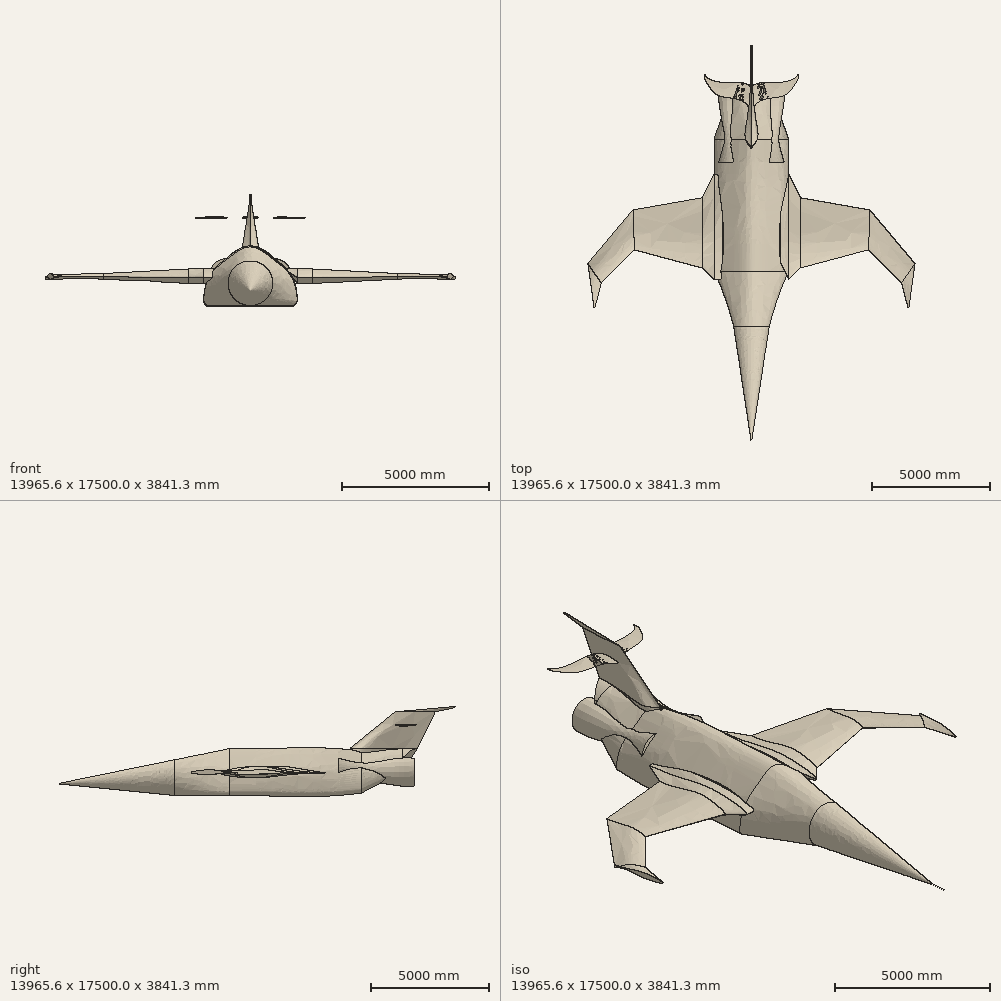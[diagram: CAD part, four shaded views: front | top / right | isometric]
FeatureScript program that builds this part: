
annotation { "Feature Type Name" : "Feature", "Feature Type Description" : "" }
export const myFeature = defineFeature(function(context is Context, id is Id, definition is map)
    precondition{}
    {
        {
            var Q0;
            Q0=qCreatedBy(makeId("Right.planeOp"),FACE);
            var sketch = newSketch(context, id + "F0", { "sketchPlane" : qUnion([Q0])});
            skLineSegment(sketch, "E0", {"start": v(0, 0) * mm, "end": v(-1750, 0) * mm});
            skLineSegment(sketch, "E1", {"start": v(-1750, 0) * mm, "end": v(-3500, 0) * mm});
            skLineSegment(sketch, "E2", {"start": v(-3500, 0) * mm, "end": v(-3500, -1000) * mm});
            skLineSegment(sketch, "E3", {"start": v(-3500, -1000) * mm, "end": v(-8500, -1000) * mm});
            skLineSegment(sketch, "E4", {"start": v(-8500, -1000) * mm, "end": v(-8500, -499.31) * mm});
            skLineSegment(sketch, "E5", {"start": v(-1151.4, 0) * mm, "end": v(-1151.4, 1000) * mm});
            skLineSegment(sketch, "E6", {"start": v(-1151.4, 1000) * mm, "end": v(-8500, -499.31) * mm});
            skLineSegment(sketch, "E7", {"start": v(-8500, -499.31) * mm, "end": v(-3500, -1000) * mm});
            skLineSegment(sketch, "E8", {"start": v(-3500, 0) * mm, "end": v(-3500, 520.82) * mm});
            skLineSegment(sketch, "E9", {"start": v(-8500, -499.31) * mm, "end": v(-8450, -499.31) * mm});
            skLineSegment(sketch, "E10", {"start": v(-8450, -499.31) * mm, "end": v(-8450, -489.1) * mm});
            skLineSegment(sketch, "E11", {"start": v(-8450, -499.31) * mm, "end": v(-8450, -504.32) * mm});
            skSolve(sketch);
        }
        {
            var Q0;
            Q0=sQuery(id+"F0.wireOp",EDGE,"E5");
            cPlane(context, id + "F1", {"entities" : qUnion([Q0]), "cplaneType" : CPlaneType.LINE_ANGLE, "offset" : 25 * mm, "angle" : 90 * degree, "oppositeDirection" : true, "width" : 150 * mm, "height" : 150 * mm});
        }
        {
            var Q0;
            Q0=qCreatedBy(id+"F1.planeOp",FACE);
            var sketch = newSketch(context, id + "F2", { "sketchPlane" : qUnion([Q0])});
            skLineSegment(sketch, "E12.top", {"start": v(-1394.2, -1000) * mm, "end": v(1394.2, -1000) * mm});
            skPoint(sketch, "E12.middle", {"position": v(0, 0) * mm});
            skFitSpline(sketch, "E13", {"points": [v(-1600, -1000) * mm, v(-848, 530) * mm, v(0, 1000) * mm, v(848, 530) * mm, v(1600, -1000) * mm], "startDerivative": vector(0, 10524.75) * mm, "endDerivative": vector(0, -10524.75) * mm});
            skArc(sketch, "E14", {"start": v(-735.27, 618.52) * mm, "mid": v(-1273.27, 435.52) * mm, "end": v(-1440.68, -107.53) * mm});
            skArc(sketch, "E15", {"start": v(1440.68, -107.53) * mm, "mid": v(1273.27, 435.52) * mm, "end": v(735.27, 618.52) * mm});
            skFitSpline(sketch, "E16.trimOffspring", {"points": [v(-1600, -1000) * mm, v(-848, 530) * mm, v(0, 1000) * mm, v(848, 530) * mm, v(1600, -1000) * mm], "startDerivative": vector(0, 10524.75) * mm, "endDerivative": vector(0, -10524.75) * mm});
            skFitSpline(sketch, "E17.trimOffspring", {"points": [v(-1600, -1000) * mm, v(-848, 530) * mm, v(0, 1000) * mm, v(848, 530) * mm, v(1600, -1000) * mm], "startDerivative": vector(0, 10524.75) * mm, "endDerivative": vector(0, -10524.75) * mm});
            skArc(sketch, "E18.filletArc", {"start": v(-1593.82, -787.83) * mm, "mid": v(-1539.85, -937.05) * mm, "end": v(-1394.2, -1000) * mm});
            skArc(sketch, "E19.filletArc", {"start": v(1394.2, -1000) * mm, "mid": v(1539.85, -937.05) * mm, "end": v(1593.82, -787.83) * mm});
            skSolve(sketch);
        }
        {
            var Q0;
            Q0=qCreatedBy(makeId("Front.planeOp"),FACE);
            var sketch = newSketch(context, id + "F3", { "sketchPlane" : qUnion([Q0])});
            skLineSegment(sketch, "E20.top", {"start": v(-1394.2, -1000) * mm, "end": v(1394.2, -1000) * mm});
            skPoint(sketch, "E20.middle", {"position": v(0, 0) * mm});
            skFitSpline(sketch, "E21", {"points": [v(-1600, -1000) * mm, v(-848, 530) * mm, v(0, 1000) * mm, v(848, 530) * mm, v(1600, -1000) * mm], "startDerivative": vector(0, 10524.75) * mm, "endDerivative": vector(0, -10524.75) * mm});
            skArc(sketch, "E22", {"start": v(-735.27, 618.52) * mm, "mid": v(-1273.27, 435.52) * mm, "end": v(-1440.68, -107.53) * mm});
            skArc(sketch, "E23", {"start": v(1440.68, -107.53) * mm, "mid": v(1273.27, 435.52) * mm, "end": v(735.27, 618.52) * mm});
            skFitSpline(sketch, "E24.trimOffspring", {"points": [v(-1600, -1000) * mm, v(-848, 530) * mm, v(0, 1000) * mm, v(848, 530) * mm, v(1600, -1000) * mm], "startDerivative": vector(0, 10524.75) * mm, "endDerivative": vector(0, -10524.75) * mm});
            skFitSpline(sketch, "E25.trimOffspring", {"points": [v(-1600, -1000) * mm, v(-848, 530) * mm, v(0, 1000) * mm, v(848, 530) * mm, v(1600, -1000) * mm], "startDerivative": vector(0, 10524.75) * mm, "endDerivative": vector(0, -10524.75) * mm});
            skArc(sketch, "E26.filletArc", {"start": v(-1593.82, -787.83) * mm, "mid": v(-1539.85, -937.05) * mm, "end": v(-1394.2, -1000) * mm});
            skArc(sketch, "E27.filletArc", {"start": v(1394.2, -1000) * mm, "mid": v(1539.85, -937.05) * mm, "end": v(1593.82, -787.83) * mm});
            skSolve(sketch);
        }
        {
            var Q0;
            Q0=qCreatedBy(makeId("Front.planeOp"),FACE);
            cPlane(context, id + "F4", {"entities" : qUnion([Q0]), "cplaneType" : CPlaneType.OFFSET, "offset" : 3500 * mm, "oppositeDirection" : true, "width" : 150 * mm, "height" : 150 * mm});
        }
        {
            var Q0;
            Q0=qCreatedBy(id+"F4.planeOp",FACE);
            var sketch = newSketch(context, id + "F5", { "sketchPlane" : qUnion([Q0])});
            skLineSegment(sketch, "E28.top", {"start": v(-1394.2, -1000) * mm, "end": v(1394.2, -1000) * mm});
            skPoint(sketch, "E28.middle", {"position": v(0, 0) * mm});
            skFitSpline(sketch, "E29", {"points": [v(-1600, -1000) * mm, v(-848, 530) * mm, v(0, 1000) * mm, v(848, 530) * mm, v(1600, -1000) * mm], "startDerivative": vector(0, 10524.75) * mm, "endDerivative": vector(0, -10524.75) * mm});
            skArc(sketch, "E30", {"start": v(-735.27, 618.52) * mm, "mid": v(-1273.27, 435.52) * mm, "end": v(-1440.68, -107.53) * mm});
            skArc(sketch, "E31", {"start": v(1440.68, -107.53) * mm, "mid": v(1273.27, 435.52) * mm, "end": v(735.27, 618.52) * mm});
            skFitSpline(sketch, "E32.trimOffspring", {"points": [v(-1600, -1000) * mm, v(-848, 530) * mm, v(0, 1000) * mm, v(848, 530) * mm, v(1600, -1000) * mm], "startDerivative": vector(0, 10524.75) * mm, "endDerivative": vector(0, -10524.75) * mm});
            skFitSpline(sketch, "E33.trimOffspring", {"points": [v(-1600, -1000) * mm, v(-848, 530) * mm, v(0, 1000) * mm, v(848, 530) * mm, v(1600, -1000) * mm], "startDerivative": vector(0, 10524.75) * mm, "endDerivative": vector(0, -10524.75) * mm});
            skArc(sketch, "E34.filletArc", {"start": v(-1593.82, -787.83) * mm, "mid": v(-1539.85, -937.05) * mm, "end": v(-1394.2, -1000) * mm});
            skArc(sketch, "E35.filletArc", {"start": v(1394.2, -1000) * mm, "mid": v(1539.85, -937.05) * mm, "end": v(1593.82, -787.83) * mm});
            skSolve(sketch);
        }
        {
            var Q0;
            Q0=qCreatedBy(makeId("Front.planeOp"),FACE);
            cPlane(context, id + "F6", {"entities" : qUnion([Q0]), "cplaneType" : CPlaneType.OFFSET, "offset" : 4500 * mm, "oppositeDirection" : true, "width" : 150 * mm, "height" : 150 * mm});
        }
        {
            var Q0;
            Q0=qCreatedBy(id+"F6.planeOp",FACE);
            var sketch = newSketch(context, id + "F7", { "sketchPlane" : qUnion([Q0])});
            skLineSegment(sketch, "E36.top", {"start": v(-1413.07, -900) * mm, "end": v(1413.07, -900) * mm});
            skPoint(sketch, "E36.middle", {"position": v(0, 0) * mm});
            skFitSpline(sketch, "E37", {"points": [v(-1600, -900) * mm, v(-784.42, 441.24) * mm, v(0, 900) * mm, v(784.42, 441.24) * mm, v(1600, -900) * mm], "startDerivative": vector(0, 9508.62) * mm, "endDerivative": vector(0, -9508.62) * mm});
            skArc(sketch, "E38", {"start": v(-719.25, 488.69) * mm, "mid": v(-1131.76, 394.84) * mm, "end": v(-1324.66, 18.33) * mm});
            skArc(sketch, "E39", {"start": v(1324.66, 18.33) * mm, "mid": v(1131.76, 394.84) * mm, "end": v(719.25, 488.69) * mm});
            skFitSpline(sketch, "E40.trimOffspring", {"points": [v(-1600, -900) * mm, v(-784.42, 441.24) * mm, v(0, 900) * mm, v(784.42, 441.24) * mm, v(1600, -900) * mm], "startDerivative": vector(0, 9508.62) * mm, "endDerivative": vector(0, -9508.62) * mm});
            skFitSpline(sketch, "E41.trimOffspring", {"points": [v(-1600, -900) * mm, v(-784.42, 441.24) * mm, v(0, 900) * mm, v(784.42, 441.24) * mm, v(1600, -900) * mm], "startDerivative": vector(0, 9508.62) * mm, "endDerivative": vector(0, -9508.62) * mm});
            skArc(sketch, "E42.filletArc", {"start": v(-1592.48, -705.43) * mm, "mid": v(-1545.4, -842.02) * mm, "end": v(-1413.07, -900) * mm});
            skArc(sketch, "E43.filletArc", {"start": v(1413.07, -900) * mm, "mid": v(1545.4, -842.02) * mm, "end": v(1592.48, -705.43) * mm});
            skLineSegment(sketch, "E44", {"start": v(-719.25, 488.69) * mm, "end": v(-1324.66, 18.33) * mm, "construction": true});
            skLineSegment(sketch, "E45", {"start": v(719.25, 488.69) * mm, "end": v(1324.66, 18.33) * mm, "construction": true});
            skSolve(sketch);
        }
        {
            var Q0;
            Q0=qCreatedBy(makeId("Front.planeOp"),FACE);
            cPlane(context, id + "F8", {"entities" : qUnion([Q0]), "cplaneType" : CPlaneType.OFFSET, "offset" : 6232.05 * mm, "oppositeDirection" : true, "width" : 150 * mm, "height" : 150 * mm});
        }
        {
            var Q0;
            Q0=qCreatedBy(id+"F8.planeOp",FACE);
            var sketch = newSketch(context, id + "F9", { "sketchPlane" : qUnion([Q0])});
            skArc(sketch, "E46", {"start": v(998.61, 52.63) * mm, "mid": v(0, 1000) * mm, "end": v(-998.61, 52.63) * mm});
            skLineSegment(sketch, "E47", {"start": v(0, 0) * mm, "end": v(-948.68, 0) * mm});
            skLineSegment(sketch, "E48", {"start": v(0, 0) * mm, "end": v(948.68, 0) * mm});
            skLineSegment(sketch, "E49", {"start": v(0, 1000) * mm, "end": v(0, 675) * mm, "construction": true});
            skLineSegment(sketch, "E50", {"start": v(0, 675) * mm, "end": v(-737.82, 675) * mm, "construction": true});
            skLineSegment(sketch, "E51", {"start": v(0, 675) * mm, "end": v(737.82, 675) * mm, "construction": true});
            skPoint(sketch, "E52.visualSharp", {"position": v(-1000, 0) * mm});
            skArc(sketch, "E52.filletArc", {"start": v(-998.61, 52.63) * mm, "mid": v(-984.96, 15.59) * mm, "end": v(-948.68, 0) * mm});
            skPoint(sketch, "E53.visualSharp", {"position": v(1000, 0) * mm});
            skArc(sketch, "E53.filletArc", {"start": v(948.68, 0) * mm, "mid": v(984.96, 15.59) * mm, "end": v(998.61, 52.63) * mm});
            skSolve(sketch);
        }
        {
            var Q0;
            Q0=makeQuery(id+"F2.imprint","IMPRINT",FACE,{"disambiguationData":[TD([[makeQuery(id+"F2.imprint","IMPRINT",EDGE,{"derivedFrom":sQuery(id+"F2.wireOp",EDGE,"E12.top")}),1.0]])]});
            var Q1;
            Q1=makeQuery(id+"F3.imprint","IMPRINT",FACE,{"disambiguationData":[TD([[makeQuery(id+"F3.imprint","IMPRINT",EDGE,{"derivedFrom":sQuery(id+"F3.wireOp",EDGE,"E20.top")}),1.0]])]});
            var Q2;
            Q2=makeQuery(id+"F5.imprint","IMPRINT",FACE,{"disambiguationData":[TD([[makeQuery(id+"F5.imprint","IMPRINT",EDGE,{"derivedFrom":sQuery(id+"F5.wireOp",EDGE,"E28.top")}),1.0]])]});
            var Q3;
            Q3=makeQuery(id+"F7.imprint","IMPRINT",FACE,{"disambiguationData":[TD([[makeQuery(id+"F7.imprint","IMPRINT",EDGE,{"derivedFrom":sQuery(id+"F7.wireOp",EDGE,"E36.top")}),1.0]])]});
            loft(context, id + "F10", {"sheetProfilesArray" : [{ "sheetProfileEntities" : qUnion([Q0]) }, { "sheetProfileEntities" : qUnion([Q1]) }, { "sheetProfileEntities" : qUnion([Q2]) }, { "sheetProfileEntities" : qUnion([Q3]) }]});
        }
        {
            var Q0;
            Q0=sQuery(id+"F7.wireOp",EDGE,"E44");
            var Q1;
            Q1=sQuery(id+"F9.wireOp",VERTEX,"E50.end");
            cPlane(context, id + "F11", {"entities" : qUnion([Q0, Q1]), "cplaneType" : CPlaneType.LINE_ANGLE, "offset" : 25 * mm, "angle" : 180 * degree, "width" : 150 * mm, "height" : 150 * mm});
        }
        {
            var Q0;
            Q0=qCreatedBy(id+"F11.planeOp",FACE);
            var sketch = newSketch(context, id + "F12", { "sketchPlane" : qUnion([Q0])});
            skLineSegment(sketch, "E54", {"start": v(-589.34, 4526.34) * mm, "end": v(-612.8, 6268.32) * mm});
            skLineSegment(sketch, "E55", {"start": v(-1354.08, 4472.19) * mm, "end": v(-612.8, 6268.32) * mm});
            skSolve(sketch);
        }
        {
            var Q0;
            Q0=sQuery(id+"F7.wireOp",EDGE,"E45");
            var Q1;
            Q1=sQuery(id+"F9.wireOp",VERTEX,"E51.end");
            cPlane(context, id + "F13", {"entities" : qUnion([Q0, Q1]), "cplaneType" : CPlaneType.LINE_ANGLE, "offset" : 25 * mm, "angle" : 0 * degree, "width" : 150 * mm, "height" : 150 * mm});
        }
        {
            var Q0;
            Q0=qCreatedBy(id+"F13.planeOp",FACE);
            var sketch = newSketch(context, id + "F14", { "sketchPlane" : qUnion([Q0])});
            skLineSegment(sketch, "E56", {"start": v(589.34, 4526.34) * mm, "end": v(612.8, 6268.32) * mm});
            skLineSegment(sketch, "E57", {"start": v(1354.08, 4472.19) * mm, "end": v(612.8, 6268.32) * mm});
            skSolve(sketch);
        }
        {
            var Q1;
            Q1=makeQuery(id+"F10.opLoft","CAP_FACE",FACE,{"disambiguationData":[OSD([makeQuery(id+"F7.imprint","IMPRINT",FACE,{"disambiguationData":[TD([[makeQuery(id+"F7.imprint","IMPRINT",EDGE,{"derivedFrom":sQuery(id+"F7.wireOp",EDGE,"E36.top")}),1.0]])]})])],"isStart":true});
            var Q2;
            Q2=makeQuery(id+"F9.imprint","IMPRINT",FACE,{"disambiguationData":[TD([[makeQuery(id+"F9.imprint","IMPRINT",EDGE,{"derivedFrom":sQuery(id+"F9.wireOp",EDGE,"E46")}),1.0]])]});
            var Q3;
            Q3=sQuery(id+"F12.wireOp",EDGE,"E54");
            var Q4;
            Q4=sQuery(id+"F14.wireOp",EDGE,"E56");
            loft(context, id + "F15", {"operationType" : NewBodyOperationType.ADD, "addGuides" : true, "sheetProfilesArray" : [{ "sheetProfileEntities" : qUnion([Q1]) }, { "sheetProfileEntities" : qUnion([Q2]) }], "guidesArray" : [{ "guideEntities" : qUnion([Q3]), "guideDerivativeType" : LoftGuideDerivativeType.DEFAULT, "guideDerivativeMagnitude" : 1 }, { "guideEntities" : qUnion([Q4]), "guideDerivativeType" : LoftGuideDerivativeType.DEFAULT, "guideDerivativeMagnitude" : 1 }]});
        }
        {
            var Q0;
            Q0=makeQuery(id+"F15.opLoft","CAP_FACE",FACE,{"disambiguationData":[OSD([makeQuery(id+"F9.imprint","IMPRINT",FACE,{"disambiguationData":[TD([[makeQuery(id+"F9.imprint","IMPRINT",EDGE,{"derivedFrom":sQuery(id+"F9.wireOp",EDGE,"E46")}),1.0]])]})])],"isStart":true});
            extrude(context, id + "F16", {"entities" : qUnion([Q0]), "operationType" : NewBodyOperationType.ADD, "depth" : 649.4 * mm, "offsetDistance" : 25 * mm});
        }
        {
            var Q0;
            Q0=qCreatedBy(makeId("Right.planeOp"),FACE);
            var sketch = newSketch(context, id + "F17", { "sketchPlane" : qUnion([Q0])});
            skLineSegment(sketch, "E58", {"start": v(0, 0) * mm, "end": v(4500, 0) * mm});
            skLineSegment(sketch, "E59", {"start": v(4500, 0) * mm, "end": v(6232.05, 0) * mm});
            skLineSegment(sketch, "E60", {"start": v(4500, 0) * mm, "end": v(4500, 1000) * mm});
            skLineSegment(sketch, "E61", {"start": v(4500, 1000) * mm, "end": v(6881.46, 1000) * mm});
            skLineSegment(sketch, "E62", {"start": v(6881.46, 1000) * mm, "end": v(6881.46, -1000) * mm});
            skLineSegment(sketch, "E63", {"start": v(6881.46, 1000) * mm, "end": v(6232.05, 0) * mm});
            skLineSegment(sketch, "E64", {"start": v(6232.05, 0) * mm, "end": v(5582.64, -1000) * mm});
            skLineSegment(sketch, "E65", {"start": v(5582.64, -1000) * mm, "end": v(6881.46, -1000) * mm});
            skSolve(sketch);
        }
        {
            var Q0;
            Q0=makeQuery(id+"F17.imprint","IMPRINT",FACE,{"disambiguationData":[TD([[makeQuery(id+"F17.imprint","IMPRINT",EDGE,{"derivedFrom":sQuery(id+"F17.wireOp",EDGE,"E62")}),-1.0]])]});
            var Q1;
            Q1=sQuery(id+"F17.wireOp",EDGE,"E61");
            revolve(context, id + "F18", {"operationType" : NewBodyOperationType.REMOVE, "entities" : qUnion([Q0]), "axis" : qUnion([Q1]), "revolveType" : RevolveType.SYMMETRIC, "oppositeDirection" : true, "angle" : 182 * degree});
        }
        {
            var Q0;
            Q0=qCreatedBy(id+"F1.planeOp",FACE);
            var sketch = newSketch(context, id + "F19", { "sketchPlane" : qUnion([Q0])});
            skLineSegment(sketch, "E66.top", {"start": v(-1394.2, -1000) * mm, "end": v(1394.2, -1000) * mm});
            skPoint(sketch, "E66.middle", {"position": v(0, 0) * mm});
            skFitSpline(sketch, "E67", {"points": [v(-1600, -1000) * mm, v(-848, 530) * mm, v(0, 1000) * mm, v(848, 530) * mm, v(1600, -1000) * mm], "startDerivative": vector(0, 10524.75) * mm, "endDerivative": vector(0, -10524.75) * mm});
            skArc(sketch, "E68.filletArc", {"start": v(-1593.82, -787.83) * mm, "mid": v(-1539.85, -937.05) * mm, "end": v(-1394.2, -1000) * mm});
            skArc(sketch, "E69.filletArc", {"start": v(1394.2, -1000) * mm, "mid": v(1539.85, -937.05) * mm, "end": v(1593.82, -787.83) * mm});
            skLineSegment(sketch, "E70", {"start": v(-1593.82, -787.83) * mm, "end": v(-1394.2, -1000) * mm, "construction": true});
            skLineSegment(sketch, "E71", {"start": v(1593.82, -787.83) * mm, "end": v(1394.2, -1000) * mm, "construction": true});
            skSolve(sketch);
        }
        {
            var Q0;
            Q0=qCreatedBy(makeId("Front.planeOp"),FACE);
            cPlane(context, id + "F20", {"entities" : qUnion([Q0]), "cplaneType" : CPlaneType.OFFSET, "offset" : 3500 * mm, "width" : 150 * mm, "height" : 150 * mm});
        }
        {
            var Q0;
            Q0=qCreatedBy(id+"F20.planeOp",FACE);
            var sketch = newSketch(context, id + "F21", { "sketchPlane" : qUnion([Q0])});
            skCircle(sketch, "E72", {"center": v(0, -239.59) * mm, "radius": 760.41 * mm});
            skLineSegment(sketch, "E73", {"start": v(0, -1000) * mm, "end": v(0, -800) * mm, "construction": true});
            skLineSegment(sketch, "E74", {"start": v(0, -800) * mm, "end": v(-513.97, -800) * mm, "construction": true});
            skLineSegment(sketch, "E75", {"start": v(0, -800) * mm, "end": v(513.97, -800) * mm, "construction": true});
            skSolve(sketch);
        }
        {
            var Q0;
            Q0=qCreatedBy(makeId("Front.planeOp"),FACE);
            cPlane(context, id + "F22", {"entities" : qUnion([Q0]), "cplaneType" : CPlaneType.OFFSET, "offset" : 8450 * mm, "width" : 150 * mm, "height" : 150 * mm});
        }
        {
            var Q0;
            Q0=qCreatedBy(id+"F22.planeOp",FACE);
            var sketch = newSketch(context, id + "F23", { "sketchPlane" : qUnion([Q0])});
            skCircle(sketch, "E76", {"center": v(0, -496.71) * mm, "radius": 7.6 * mm});
            skSolve(sketch);
        }
        {
            var Q0;
            Q0=sQuery(id+"F19.wireOp",EDGE,"E70");
            var Q1;
            Q1=sQuery(id+"F21.wireOp",VERTEX,"E74.end");
            cPlane(context, id + "F24", {"entities" : qUnion([Q0, Q1]), "cplaneType" : CPlaneType.LINE_ANGLE, "offset" : 25 * mm, "angle" : 0 * degree, "width" : 150 * mm, "height" : 150 * mm});
        }
        {
            var Q0;
            Q0=qCreatedBy(id+"F24.planeOp",FACE);
            var sketch = newSketch(context, id + "F25", { "sketchPlane" : qUnion([Q0])});
            skLineSegment(sketch, "E77", {"start": v(3032.27, -230.44) * mm, "end": v(558.11, 518.4) * mm});
            skLineSegment(sketch, "E78", {"start": v(3032.27, -230.44) * mm, "end": v(558.11, 227.09) * mm});
            skSolve(sketch);
        }
        {
            var Q0;
            Q0=sQuery(id+"F19.wireOp",EDGE,"E71");
            var Q1;
            Q1=sQuery(id+"F21.wireOp",VERTEX,"E75.end");
            cPlane(context, id + "F26", {"entities" : qUnion([Q0, Q1]), "cplaneType" : CPlaneType.LINE_ANGLE, "offset" : 25 * mm, "angle" : 180 * degree, "width" : 150 * mm, "height" : 150 * mm});
        }
        {
            var Q0;
            Q0=qCreatedBy(id+"F26.planeOp",FACE);
            var sketch = newSketch(context, id + "F27", { "sketchPlane" : qUnion([Q0])});
            skLineSegment(sketch, "E79", {"start": v(-3032.27, -230.44) * mm, "end": v(-558.11, 518.4) * mm});
            skLineSegment(sketch, "E80", {"start": v(-3032.27, -230.44) * mm, "end": v(-558.11, 227.09) * mm});
            skSolve(sketch);
        }
        {
            var Q1;
            Q1=makeQuery(id+"F19.imprint","IMPRINT",FACE,{"disambiguationData":[TD([[makeQuery(id+"F19.imprint","IMPRINT",EDGE,{"derivedFrom":sQuery(id+"F19.wireOp",EDGE,"E66.top")}),1.0]])]});
            var Q2;
            Q2=makeQuery(id+"F21.imprint","IMPRINT",FACE,{"disambiguationData":[TD([[makeQuery(id+"F21.imprint","IMPRINT",EDGE,{"derivedFrom":sQuery(id+"F21.wireOp",EDGE,"E72")}),1.0]])]});
            var Q3;
            Q3=sQuery(id+"F25.wireOp",EDGE,"E77");
            var Q4;
            Q4=sQuery(id+"F27.wireOp",EDGE,"E79");
            loft(context, id + "F28", {"operationType" : NewBodyOperationType.ADD, "addGuides" : true, "sheetProfilesArray" : [{ "sheetProfileEntities" : qUnion([Q1]) }, { "sheetProfileEntities" : qUnion([Q2]) }], "guidesArray" : [{ "guideEntities" : qUnion([Q3]), "guideDerivativeType" : LoftGuideDerivativeType.DEFAULT, "guideDerivativeMagnitude" : 1 }, { "guideEntities" : qUnion([Q4]), "guideDerivativeType" : LoftGuideDerivativeType.DEFAULT, "guideDerivativeMagnitude" : 1 }]});
        }
        {
            var Q1;
            Q1=makeQuery(id+"F28.opLoft","CAP_FACE",FACE,{"disambiguationData":[OSD([makeQuery(id+"F21.imprint","IMPRINT",FACE,{"disambiguationData":[TD([[makeQuery(id+"F21.imprint","IMPRINT",EDGE,{"derivedFrom":sQuery(id+"F21.wireOp",EDGE,"E72")}),1.0]])]})])],"isStart":true});
            var Q2;
            Q2=makeQuery(id+"F23.imprint","IMPRINT",FACE,{"disambiguationData":[TD([[makeQuery(id+"F23.imprint","IMPRINT",EDGE,{"derivedFrom":sQuery(id+"F23.wireOp",EDGE,"E76")}),1.0]])]});
            loft(context, id + "F29", {"operationType" : NewBodyOperationType.ADD, "sheetProfilesArray" : [{ "sheetProfileEntities" : qUnion([Q1]) }, { "sheetProfileEntities" : qUnion([Q2]) }]});
        }
        {
            var Q0;
            Q0=makeQuery(id+"F29.opLoft","CAP_FACE",FACE,{"disambiguationData":[OSD([makeQuery(id+"F23.imprint","IMPRINT",FACE,{"disambiguationData":[TD([[makeQuery(id+"F23.imprint","IMPRINT",EDGE,{"derivedFrom":sQuery(id+"F23.wireOp",EDGE,"E76")}),1.0]])]})])],"isStart":true});
            extrude(context, id + "F30", {"entities" : qUnion([Q0]), "operationType" : NewBodyOperationType.ADD, "depth" : 550 * mm, "offsetDistance" : 25 * mm});
        }
        {
            var Q0;
            Q0=qCreatedBy(makeId("Front.planeOp"),FACE);
            cPlane(context, id + "F31", {"entities" : qUnion([Q0]), "cplaneType" : CPlaneType.OFFSET, "offset" : 3500 * mm, "oppositeDirection" : true, "width" : 150 * mm, "height" : 150 * mm});
        }
        {
            var Q0;
            Q0=qCreatedBy(id+"F31.planeOp",FACE);
            var sketch = newSketch(context, id + "F32", { "sketchPlane" : qUnion([Q0])});
            skCircle(sketch, "E81", {"center": v(-800, 0) * mm, "radius": 600 * mm});
            skCircle(sketch, "E82", {"center": v(800, 0) * mm, "radius": 600 * mm});
            skSolve(sketch);
        }
        {
            var Q0;
            Q0=qCreatedBy(makeId("Front.planeOp"),FACE);
            cPlane(context, id + "F33", {"entities" : qUnion([Q0]), "cplaneType" : CPlaneType.OFFSET, "offset" : 4500 * mm, "oppositeDirection" : true, "width" : 150 * mm, "height" : 150 * mm});
        }
        {
            var Q0;
            Q0=qCreatedBy(id+"F33.planeOp",FACE);
            var sketch = newSketch(context, id + "F34", { "sketchPlane" : qUnion([Q0])});
            skCircle(sketch, "E83", {"center": v(-800, 0) * mm, "radius": 400 * mm});
            skCircle(sketch, "E84", {"center": v(800, 0) * mm, "radius": 400 * mm});
            skSolve(sketch);
        }
        {
            var Q0;
            Q0=qCreatedBy(makeId("Front.planeOp"),FACE);
            cPlane(context, id + "F35", {"entities" : qUnion([Q0]), "cplaneType" : CPlaneType.OFFSET, "offset" : 6232.05 * mm, "oppositeDirection" : true, "width" : 150 * mm, "height" : 150 * mm});
        }
        {
            var Q0;
            Q0=qCreatedBy(id+"F35.planeOp",FACE);
            var sketch = newSketch(context, id + "F36", { "sketchPlane" : qUnion([Q0])});
            skCircle(sketch, "E85", {"center": v(-800, 0) * mm, "radius": 600 * mm});
            skCircle(sketch, "E86", {"center": v(800, 0) * mm, "radius": 600 * mm});
            skSolve(sketch);
        }
        {
            var Q0;
            Q0=qCreatedBy(makeId("Front.planeOp"),FACE);
            cPlane(context, id + "F37", {"entities" : qUnion([Q0]), "cplaneType" : CPlaneType.OFFSET, "offset" : 6732.05 * mm, "oppositeDirection" : true, "width" : 150 * mm, "height" : 150 * mm});
        }
        {
            var Q0;
            Q0=qCreatedBy(id+"F37.planeOp",FACE);
            var sketch = newSketch(context, id + "F38", { "sketchPlane" : qUnion([Q0])});
            skCircle(sketch, "E87", {"center": v(-800, 0) * mm, "radius": 600 * mm});
            skCircle(sketch, "E88", {"center": v(800, 0) * mm, "radius": 600 * mm});
            skSolve(sketch);
        }
        {
            var Q0;
            Q0=makeQuery(id+"F32.imprint","IMPRINT",FACE,{"disambiguationData":[TD([[makeQuery(id+"F32.imprint","IMPRINT",EDGE,{"derivedFrom":sQuery(id+"F32.wireOp",EDGE,"E81")}),1.0]])]});
            var Q1;
            Q1=makeQuery(id+"F34.imprint","IMPRINT",FACE,{"disambiguationData":[TD([[makeQuery(id+"F34.imprint","IMPRINT",EDGE,{"derivedFrom":sQuery(id+"F34.wireOp",EDGE,"E83")}),1.0]])]});
            var Q2;
            Q2=makeQuery(id+"F36.imprint","IMPRINT",FACE,{"disambiguationData":[TD([[makeQuery(id+"F36.imprint","IMPRINT",EDGE,{"derivedFrom":sQuery(id+"F36.wireOp",EDGE,"E85")}),1.0]])]});
            var Q3;
            Q3=makeQuery(id+"F38.imprint","IMPRINT",FACE,{"disambiguationData":[TD([[makeQuery(id+"F38.imprint","IMPRINT",EDGE,{"derivedFrom":sQuery(id+"F38.wireOp",EDGE,"E87")}),1.0]])]});
            loft(context, id + "F39", {"sheetProfilesArray" : [{ "sheetProfileEntities" : qUnion([Q0]) }, { "sheetProfileEntities" : qUnion([Q1]) }, { "sheetProfileEntities" : qUnion([Q2]) }, { "sheetProfileEntities" : qUnion([Q3]) }]});
        }
        {
            var Q0;
            Q0=makeQuery(id+"F32.imprint","IMPRINT",FACE,{"disambiguationData":[TD([[makeQuery(id+"F32.imprint","IMPRINT",EDGE,{"derivedFrom":sQuery(id+"F32.wireOp",EDGE,"E82")}),1.0]])]});
            var Q1;
            Q1=makeQuery(id+"F34.imprint","IMPRINT",FACE,{"disambiguationData":[TD([[makeQuery(id+"F34.imprint","IMPRINT",EDGE,{"derivedFrom":sQuery(id+"F34.wireOp",EDGE,"E84")}),1.0]])]});
            var Q2;
            Q2=makeQuery(id+"F36.imprint","IMPRINT",FACE,{"disambiguationData":[TD([[makeQuery(id+"F36.imprint","IMPRINT",EDGE,{"derivedFrom":sQuery(id+"F36.wireOp",EDGE,"E86")}),1.0]])]});
            var Q3;
            Q3=makeQuery(id+"F38.imprint","IMPRINT",FACE,{"disambiguationData":[TD([[makeQuery(id+"F38.imprint","IMPRINT",EDGE,{"derivedFrom":sQuery(id+"F38.wireOp",EDGE,"E88")}),1.0]])]});
            loft(context, id + "F40", {"sheetProfilesArray" : [{ "sheetProfileEntities" : qUnion([Q0]) }, { "sheetProfileEntities" : qUnion([Q1]) }, { "sheetProfileEntities" : qUnion([Q2]) }, { "sheetProfileEntities" : qUnion([Q3]) }]});
        }
        {
            var Q0;
            Q0=qCreatedBy(makeId("Top.planeOp"),FACE);
            var sketch = newSketch(context, id + "F41", { "sketchPlane" : qUnion([Q0])});
            skLineSegment(sketch, "E89", {"start": v(0, 0) * mm, "end": v(-1250, 0) * mm});
            skLineSegment(sketch, "E90", {"start": v(-1250, 0) * mm, "end": v(-2100, 0) * mm});
            skLineSegment(sketch, "E91", {"start": v(-2100, 0) * mm, "end": v(-2100, -1000) * mm});
            skLineSegment(sketch, "E92", {"start": v(-2100, 0) * mm, "end": v(-2100, 2000) * mm});
            skLineSegment(sketch, "E93", {"start": v(-2100, -1000) * mm, "end": v(-4997.78, -223.54) * mm});
            skLineSegment(sketch, "E94", {"start": v(-2100, 2000) * mm, "end": v(-5054.42, 1479.06) * mm});
            skLineSegment(sketch, "E95", {"start": v(-4997.78, -223.54) * mm, "end": v(-5054.42, 1479.06) * mm});
            skLineSegment(sketch, "E96", {"start": v(-4997.78, -223.54) * mm, "end": v(-6412, -1637.76) * mm});
            skLineSegment(sketch, "E97", {"start": v(-5054.42, 1479.06) * mm, "end": v(-6982.79, -819.08) * mm});
            skLineSegment(sketch, "E98", {"start": v(-6412, -1637.76) * mm, "end": v(-6982.79, -819.08) * mm});
            skLineSegment(sketch, "E99", {"start": v(-6412, -1637.76) * mm, "end": v(-6704.44, -2799.61) * mm});
            skLineSegment(sketch, "E100", {"start": v(-6704.44, -2799.61) * mm, "end": v(-6982.79, -819.08) * mm});
            skLineSegment(sketch, "E101", {"start": v(0, 0) * mm, "end": v(1250, 0) * mm});
            skLineSegment(sketch, "E102", {"start": v(1250, 0) * mm, "end": v(2100, 0) * mm});
            skLineSegment(sketch, "E103", {"start": v(2100, 0) * mm, "end": v(2100, -1000) * mm});
            skLineSegment(sketch, "E104", {"start": v(2100, 0) * mm, "end": v(2100, 2000) * mm});
            skLineSegment(sketch, "E105", {"start": v(2100, -1000) * mm, "end": v(4997.78, -223.54) * mm});
            skLineSegment(sketch, "E106", {"start": v(2100, 2000) * mm, "end": v(5054.42, 1479.06) * mm});
            skLineSegment(sketch, "E107", {"start": v(4997.78, -223.54) * mm, "end": v(5054.42, 1479.06) * mm});
            skLineSegment(sketch, "E108", {"start": v(4997.78, -223.54) * mm, "end": v(6412, -1637.76) * mm});
            skLineSegment(sketch, "E109", {"start": v(5054.42, 1479.06) * mm, "end": v(6982.79, -819.08) * mm});
            skLineSegment(sketch, "E110", {"start": v(6412, -1637.76) * mm, "end": v(6982.79, -819.08) * mm});
            skLineSegment(sketch, "E111", {"start": v(6412, -1637.76) * mm, "end": v(6704.44, -2799.61) * mm});
            skLineSegment(sketch, "E112", {"start": v(6704.44, -2799.61) * mm, "end": v(6982.79, -819.08) * mm});
            skSolve(sketch);
        }
        {
            var Q0;
            Q0=qCreatedBy(makeId("Right.planeOp"),FACE);
            var sketch = newSketch(context, id + "F42", { "sketchPlane" : qUnion([Q0])});
            skFitSpline(sketch, "E113", {"points": [v(-1500, -50) * mm, v(0, 250) * mm, v(3000, -50) * mm, v(0, -250) * mm, v(-1500, -50) * mm]});
            skSolve(sketch);
        }
        {
            var Q0;
            Q0=qCreatedBy(makeId("Right.planeOp"),FACE);
            cPlane(context, id + "F43", {"entities" : qUnion([Q0]), "cplaneType" : CPlaneType.OFFSET, "offset" : 1600 * mm, "oppositeDirection" : true, "width" : 150 * mm, "height" : 150 * mm});
        }
        {
            var Q0;
            Q0=qCreatedBy(id+"F43.planeOp",FACE);
            var sketch = newSketch(context, id + "F44", { "sketchPlane" : qUnion([Q0])});
            skFitSpline(sketch, "E114", {"points": [v(-1500, -50) * mm, v(0, 250) * mm, v(3000, -50) * mm], "startDerivative": vector(0, 887.04) * mm, "endDerivative": vector(7705.35, -256.85) * mm});
            skFitSpline(sketch, "E115", {"points": [v(-1500, -50) * mm, v(0, -250) * mm, v(3000, -50) * mm], "startDerivative": vector(0, -722.87) * mm, "endDerivative": vector(7692.49, -256.42) * mm});
            skSolve(sketch);
        }
        {
            var Q0;
            Q0=qCreatedBy(makeId("Right.planeOp"),FACE);
            cPlane(context, id + "F45", {"entities" : qUnion([Q0]), "cplaneType" : CPlaneType.OFFSET, "offset" : 1600 * mm, "width" : 150 * mm, "height" : 150 * mm});
        }
        {
            var Q0;
            Q0=qCreatedBy(id+"F45.planeOp",FACE);
            var sketch = newSketch(context, id + "F46", { "sketchPlane" : qUnion([Q0])});
            skFitSpline(sketch, "E116", {"points": [v(-1500, -50) * mm, v(0, 250) * mm, v(3000, -50) * mm], "startDerivative": vector(0, 887.04) * mm, "endDerivative": vector(7705.35, -256.85) * mm});
            skFitSpline(sketch, "E117", {"points": [v(-1500, -50) * mm, v(0, -250) * mm, v(3000, -50) * mm], "startDerivative": vector(0, -722.87) * mm, "endDerivative": vector(7692.49, -256.42) * mm});
            skSolve(sketch);
        }
        {
            var Q0;
            Q0=qCreatedBy(makeId("Right.planeOp"),FACE);
            cPlane(context, id + "F47", {"entities" : qUnion([Q0]), "cplaneType" : CPlaneType.OFFSET, "offset" : 2100 * mm, "oppositeDirection" : true, "width" : 150 * mm, "height" : 150 * mm});
        }
        {
            var Q0;
            Q0=qCreatedBy(id+"F47.planeOp",FACE);
            var sketch = newSketch(context, id + "F48", { "sketchPlane" : qUnion([Q0])});
            skFitSpline(sketch, "E118", {"points": [v(-1000, -36) * mm, v(0, 250) * mm, v(2000, -36) * mm], "startDerivative": vector(0, 574.5) * mm, "endDerivative": vector(5152.5, -185.5) * mm});
            skFitSpline(sketch, "E119", {"points": [v(-1000, -36) * mm, v(0, -250) * mm, v(2000, -36) * mm], "startDerivative": vector(0, -699.11) * mm, "endDerivative": vector(5139.1, -185) * mm});
            skSolve(sketch);
        }
        {
            var Q0;
            Q0=qCreatedBy(makeId("Right.planeOp"),FACE);
            cPlane(context, id + "F49", {"entities" : qUnion([Q0]), "cplaneType" : CPlaneType.OFFSET, "offset" : 2100 * mm, "width" : 150 * mm, "height" : 150 * mm});
        }
        {
            var Q0;
            Q0=qCreatedBy(id+"F49.planeOp",FACE);
            var sketch = newSketch(context, id + "F50", { "sketchPlane" : qUnion([Q0])});
            skFitSpline(sketch, "E120", {"points": [v(-1000, -36) * mm, v(0, 250) * mm, v(2000, -36) * mm], "startDerivative": vector(0, 574.5) * mm, "endDerivative": vector(5152.5, -185.5) * mm});
            skFitSpline(sketch, "E121", {"points": [v(-1000, -36) * mm, v(0, -250) * mm, v(2000, -36) * mm], "startDerivative": vector(0, -699.11) * mm, "endDerivative": vector(5139.1, -185) * mm});
            skSolve(sketch);
        }
        {
            var Q0;
            Q0=sQuery(id+"F41.wireOp",EDGE,"E95");
            cPlane(context, id + "F51", {"entities" : qUnion([Q0]), "cplaneType" : CPlaneType.LINE_ANGLE, "offset" : 25 * mm, "angle" : 90 * degree, "oppositeDirection" : true, "width" : 150 * mm, "height" : 150 * mm});
        }
        {
            var Q0;
            Q0=qCreatedBy(id+"F51.planeOp",FACE);
            var sketch = newSketch(context, id + "F52", { "sketchPlane" : qUnion([Q0])});
            skFitSpline(sketch, "E122", {"points": [v(57.23, -18) * mm, v(-442.77, 100) * mm, v(-1646.3, -18) * mm], "startDerivative": vector(0, 311.71) * mm, "endDerivative": vector(-2981.97, -89.2) * mm});
            skFitSpline(sketch, "E123", {"points": [v(57.23, -18) * mm, v(-442.77, -100) * mm, v(-1646.3, -18) * mm], "startDerivative": vector(0, -370) * mm, "endDerivative": vector(-2975.3, -89) * mm});
            skSolve(sketch);
        }
        {
            var Q0;
            Q0=sQuery(id+"F41.wireOp",EDGE,"E107");
            cPlane(context, id + "F53", {"entities" : qUnion([Q0]), "cplaneType" : CPlaneType.LINE_ANGLE, "offset" : 25 * mm, "angle" : 90 * degree, "width" : 150 * mm, "height" : 150 * mm});
        }
        {
            var Q0;
            Q0=qCreatedBy(id+"F53.planeOp",FACE);
            var sketch = newSketch(context, id + "F54", { "sketchPlane" : qUnion([Q0])});
            skFitSpline(sketch, "E124", {"points": [v(-57.23, -18) * mm, v(442.77, 100) * mm, v(1646.3, -18) * mm], "startDerivative": vector(0, 311.71) * mm, "endDerivative": vector(2981.97, -89.2) * mm});
            skFitSpline(sketch, "E125", {"points": [v(-57.23, -18) * mm, v(442.77, -100) * mm, v(1646.3, -18) * mm], "startDerivative": vector(0, -370) * mm, "endDerivative": vector(2975.3, -89) * mm});
            skSolve(sketch);
        }
        {
            var Q0;
            Q0=sQuery(id+"F41.wireOp",EDGE,"E98");
            cPlane(context, id + "F55", {"entities" : qUnion([Q0]), "cplaneType" : CPlaneType.LINE_ANGLE, "offset" : 25 * mm, "angle" : 90 * degree, "oppositeDirection" : true, "width" : 150 * mm, "height" : 150 * mm});
        }
        {
            var Q0;
            Q0=qCreatedBy(id+"F55.planeOp",FACE);
            var sketch = newSketch(context, id + "F56", { "sketchPlane" : qUnion([Q0])});
            skFitSpline(sketch, "E126", {"points": [v(-2323.74, 0) * mm, v(-2822.75, 50) * mm, v(-3321.76, -125) * mm], "startDerivative": vector(-1017.94, 211.55) * mm, "endDerivative": vector(-978.27, -458.6) * mm});
            skFitSpline(sketch, "E127", {"points": [v(-2323.74, 0) * mm, v(-2822.75, -50) * mm, v(-3321.76, -125) * mm], "startDerivative": vector(-1000.33, -87.77) * mm, "endDerivative": vector(-995.7, -162.2) * mm});
            skSolve(sketch);
        }
        {
            var Q0;
            Q0=sQuery(id+"F41.wireOp",EDGE,"E110");
            cPlane(context, id + "F57", {"entities" : qUnion([Q0]), "cplaneType" : CPlaneType.LINE_ANGLE, "offset" : 25 * mm, "angle" : 90 * degree, "width" : 150 * mm, "height" : 150 * mm});
        }
        {
            var Q0;
            Q0=qCreatedBy(id+"F57.planeOp",FACE);
            var sketch = newSketch(context, id + "F58", { "sketchPlane" : qUnion([Q0])});
            skFitSpline(sketch, "E128", {"points": [v(2323.74, 0) * mm, v(2822.75, 50) * mm, v(3321.76, -125) * mm], "startDerivative": vector(1017.94, 211.55) * mm, "endDerivative": vector(978.27, -458.6) * mm});
            skFitSpline(sketch, "E129", {"points": [v(2323.74, 0) * mm, v(2822.75, -50) * mm, v(3321.76, -125) * mm], "startDerivative": vector(1000.33, -87.77) * mm, "endDerivative": vector(995.7, -162.2) * mm});
            skSolve(sketch);
        }
        {
            var Q0;
            Q0=sQuery(id+"F41.wireOp",EDGE,"E100");
            cPlane(context, id + "F59", {"entities" : qUnion([Q0]), "cplaneType" : CPlaneType.LINE_ANGLE, "offset" : 25 * mm, "angle" : 90 * degree, "oppositeDirection" : true, "width" : 150 * mm, "height" : 150 * mm});
        }
        {
            var Q0;
            Q0=qCreatedBy(id+"F59.planeOp",FACE);
            var sketch = newSketch(context, id + "F60", { "sketchPlane" : qUnion([Q0])});
            skFitSpline(sketch, "E130", {"points": [v(1839.3, -18) * mm, v(1039.3, 100) * mm, v(-160.7, -18) * mm], "startDerivative": vector(0, 273.2) * mm, "endDerivative": vector(-3274.07, -98.22) * mm});
            skFitSpline(sketch, "E131", {"points": [v(1839.3, -18) * mm, v(1039.3, -100) * mm, v(-160.7, -18) * mm], "startDerivative": vector(0, -323.44) * mm, "endDerivative": vector(-3271.82, -98.15) * mm});
            skSolve(sketch);
        }
        {
            var Q0;
            Q0=sQuery(id+"F41.wireOp",EDGE,"E112");
            cPlane(context, id + "F61", {"entities" : qUnion([Q0]), "cplaneType" : CPlaneType.LINE_ANGLE, "offset" : 25 * mm, "angle" : 90 * degree, "width" : 150 * mm, "height" : 150 * mm});
        }
        {
            var Q0;
            Q0=qCreatedBy(id+"F61.planeOp",FACE);
            var sketch = newSketch(context, id + "F62", { "sketchPlane" : qUnion([Q0])});
            skFitSpline(sketch, "E132", {"points": [v(-1839.3, -18) * mm, v(-1039.3, 100) * mm, v(160.7, -18) * mm], "startDerivative": vector(0, 273.2) * mm, "endDerivative": vector(3274.07, -98.22) * mm});
            skFitSpline(sketch, "E133", {"points": [v(-1839.3, -18) * mm, v(-1039.3, -100) * mm, v(160.7, -18) * mm], "startDerivative": vector(0, -323.44) * mm, "endDerivative": vector(3271.82, -98.15) * mm});
            skSolve(sketch);
        }
        {
            var Q0;
            Q0=qSketchRegion(id+"F42",true);
            extrude(context, id + "F63", {"entities" : qUnion([Q0]), "endBound" : BoundingType.SYMMETRIC, "depth" : 2500 * mm, "offsetDistance" : 25 * mm});
        }
        {
            var Q1;
            Q1=makeQuery(id+"F63.opExtrude","CAP_FACE",FACE,{"disambiguationData":[OSD([sQuery(id+"F42.wireOp",EDGE,"E113")])],"isStart":true});
            var Q2;
            {var subQ0=sQuery(id+"F44.wireOp",EDGE,"E114");Q2=makeQuery(id+"F44.imprint","IMPRINT",FACE,{"disambiguationData":[TD([[makeQuery(id+"F44.imprint","IMPRINT",EDGE,{"derivedFrom":subQ0}),-1.0]])]});}
            loft(context, id + "F64", {"operationType" : NewBodyOperationType.ADD, "sheetProfilesArray" : [{ "sheetProfileEntities" : qUnion([Q1]) }, { "sheetProfileEntities" : qUnion([Q2]) }]});
        }
        {
            var Q1;
            Q1=makeQuery(id+"F63.opExtrude","CAP_FACE",FACE,{"disambiguationData":[OSD([sQuery(id+"F42.wireOp",EDGE,"E113")])],"isStart":false});
            var Q2;
            {var subQ0=sQuery(id+"F46.wireOp",EDGE,"E116");Q2=makeQuery(id+"F46.imprint","IMPRINT",FACE,{"disambiguationData":[TD([[makeQuery(id+"F46.imprint","IMPRINT",EDGE,{"derivedFrom":subQ0}),-1.0]])]});}
            loft(context, id + "F65", {"operationType" : NewBodyOperationType.ADD, "sheetProfilesArray" : [{ "sheetProfileEntities" : qUnion([Q1]) }, { "sheetProfileEntities" : qUnion([Q2]) }]});
        }
        {
            var Q1;
            {var subQ0=sQuery(id+"F44.wireOp",EDGE,"E114");Q1=makeQuery(id+"F64.opLoft","CAP_FACE",FACE,{"disambiguationData":[OSD([makeQuery(id+"F44.imprint","IMPRINT",FACE,{"disambiguationData":[TD([[makeQuery(id+"F44.imprint","IMPRINT",EDGE,{"derivedFrom":subQ0}),-1.0]])]})])],"isStart":true});}
            var Q2;
            {var subQ0=sQuery(id+"F48.wireOp",EDGE,"E118");Q2=makeQuery(id+"F48.imprint","IMPRINT",FACE,{"disambiguationData":[TD([[makeQuery(id+"F48.imprint","IMPRINT",EDGE,{"derivedFrom":subQ0}),-1.0]])]});}
            loft(context, id + "F66", {"operationType" : NewBodyOperationType.ADD, "sheetProfilesArray" : [{ "sheetProfileEntities" : qUnion([Q1]) }, { "sheetProfileEntities" : qUnion([Q2]) }]});
        }
        {
            var Q1;
            {var subQ0=sQuery(id+"F46.wireOp",EDGE,"E116");Q1=makeQuery(id+"F65.opLoft","CAP_FACE",FACE,{"disambiguationData":[OSD([makeQuery(id+"F46.imprint","IMPRINT",FACE,{"disambiguationData":[TD([[makeQuery(id+"F46.imprint","IMPRINT",EDGE,{"derivedFrom":subQ0}),-1.0]])]})])],"isStart":true});}
            var Q2;
            {var subQ0=sQuery(id+"F50.wireOp",EDGE,"E120");Q2=makeQuery(id+"F50.imprint","IMPRINT",FACE,{"disambiguationData":[TD([[makeQuery(id+"F50.imprint","IMPRINT",EDGE,{"derivedFrom":subQ0}),-1.0]])]});}
            loft(context, id + "F67", {"operationType" : NewBodyOperationType.ADD, "sheetProfilesArray" : [{ "sheetProfileEntities" : qUnion([Q1]) }, { "sheetProfileEntities" : qUnion([Q2]) }]});
        }
        {
            var Q1;
            {var subQ0=sQuery(id+"F48.wireOp",EDGE,"E118");Q1=makeQuery(id+"F66.opLoft","CAP_FACE",FACE,{"disambiguationData":[OSD([makeQuery(id+"F48.imprint","IMPRINT",FACE,{"disambiguationData":[TD([[makeQuery(id+"F48.imprint","IMPRINT",EDGE,{"derivedFrom":subQ0}),-1.0]])]})])],"isStart":true});}
            var Q2;
            {var subQ0=sQuery(id+"F52.wireOp",EDGE,"E122");Q2=makeQuery(id+"F52.imprint","IMPRINT",FACE,{"disambiguationData":[TD([[makeQuery(id+"F52.imprint","IMPRINT",EDGE,{"derivedFrom":subQ0}),1.0]])]});}
            loft(context, id + "F68", {"operationType" : NewBodyOperationType.ADD, "sheetProfilesArray" : [{ "sheetProfileEntities" : qUnion([Q1]) }, { "sheetProfileEntities" : qUnion([Q2]) }]});
        }
        {
            var Q1;
            {var subQ0=sQuery(id+"F50.wireOp",EDGE,"E120");Q1=makeQuery(id+"F67.opLoft","CAP_FACE",FACE,{"disambiguationData":[OSD([makeQuery(id+"F50.imprint","IMPRINT",FACE,{"disambiguationData":[TD([[makeQuery(id+"F50.imprint","IMPRINT",EDGE,{"derivedFrom":subQ0}),-1.0]])]})])],"isStart":true});}
            var Q2;
            {var subQ0=sQuery(id+"F54.wireOp",EDGE,"E124");Q2=makeQuery(id+"F54.imprint","IMPRINT",FACE,{"disambiguationData":[TD([[makeQuery(id+"F54.imprint","IMPRINT",EDGE,{"derivedFrom":subQ0}),-1.0]])]});}
            loft(context, id + "F69", {"operationType" : NewBodyOperationType.ADD, "sheetProfilesArray" : [{ "sheetProfileEntities" : qUnion([Q1]) }, { "sheetProfileEntities" : qUnion([Q2]) }]});
        }
        {
            var Q1;
            {var subQ0=sQuery(id+"F52.wireOp",EDGE,"E122");Q1=makeQuery(id+"F68.opLoft","CAP_FACE",FACE,{"disambiguationData":[OSD([makeQuery(id+"F52.imprint","IMPRINT",FACE,{"disambiguationData":[TD([[makeQuery(id+"F52.imprint","IMPRINT",EDGE,{"derivedFrom":subQ0}),1.0]])]})])],"isStart":true});}
            var Q2;
            Q2=makeQuery(id+"F56.imprint","IMPRINT",FACE,{"disambiguationData":[TD([[makeQuery(id+"F56.imprint","IMPRINT",EDGE,{"derivedFrom":sQuery(id+"F56.wireOp",EDGE,"E126")}),1.0]])]});
            loft(context, id + "F70", {"operationType" : NewBodyOperationType.ADD, "sheetProfilesArray" : [{ "sheetProfileEntities" : qUnion([Q1]) }, { "sheetProfileEntities" : qUnion([Q2]) }]});
        }
        {
            var Q1;
            {var subQ0=sQuery(id+"F54.wireOp",EDGE,"E124");Q1=makeQuery(id+"F69.opLoft","CAP_FACE",FACE,{"disambiguationData":[OSD([makeQuery(id+"F54.imprint","IMPRINT",FACE,{"disambiguationData":[TD([[makeQuery(id+"F54.imprint","IMPRINT",EDGE,{"derivedFrom":subQ0}),-1.0]])]})])],"isStart":true});}
            var Q2;
            Q2=makeQuery(id+"F58.imprint","IMPRINT",FACE,{"disambiguationData":[TD([[makeQuery(id+"F58.imprint","IMPRINT",EDGE,{"derivedFrom":sQuery(id+"F58.wireOp",EDGE,"E128")}),-1.0]])]});
            loft(context, id + "F71", {"operationType" : NewBodyOperationType.ADD, "sheetProfilesArray" : [{ "sheetProfileEntities" : qUnion([Q1]) }, { "sheetProfileEntities" : qUnion([Q2]) }]});
        }
        {
            var Q1;
            Q1=makeQuery(id+"F70.opLoft","CAP_FACE",FACE,{"disambiguationData":[OSD([makeQuery(id+"F56.imprint","IMPRINT",FACE,{"disambiguationData":[TD([[makeQuery(id+"F56.imprint","IMPRINT",EDGE,{"derivedFrom":sQuery(id+"F56.wireOp",EDGE,"E126")}),1.0]])]})])],"isStart":true});
            var Q2;
            {var subQ0=sQuery(id+"F60.wireOp",EDGE,"E130");Q2=makeQuery(id+"F60.imprint","IMPRINT",FACE,{"disambiguationData":[TD([[makeQuery(id+"F60.imprint","IMPRINT",EDGE,{"derivedFrom":subQ0}),1.0]])]});}
            loft(context, id + "F72", {"operationType" : NewBodyOperationType.ADD, "sheetProfilesArray" : [{ "sheetProfileEntities" : qUnion([Q1]) }, { "sheetProfileEntities" : qUnion([Q2]) }]});
        }
        {
            var Q1;
            Q1=makeQuery(id+"F71.opLoft","CAP_FACE",FACE,{"disambiguationData":[OSD([makeQuery(id+"F58.imprint","IMPRINT",FACE,{"disambiguationData":[TD([[makeQuery(id+"F58.imprint","IMPRINT",EDGE,{"derivedFrom":sQuery(id+"F58.wireOp",EDGE,"E128")}),-1.0]])]})])],"isStart":true});
            var Q2;
            {var subQ0=sQuery(id+"F62.wireOp",EDGE,"E132");Q2=makeQuery(id+"F62.imprint","IMPRINT",FACE,{"disambiguationData":[TD([[makeQuery(id+"F62.imprint","IMPRINT",EDGE,{"derivedFrom":subQ0}),-1.0]])]});}
            loft(context, id + "F73", {"operationType" : NewBodyOperationType.ADD, "sheetProfilesArray" : [{ "sheetProfileEntities" : qUnion([Q1]) }, { "sheetProfileEntities" : qUnion([Q2]) }]});
        }
        {
            var Q0;
            Q0=qCreatedBy(makeId("Right.planeOp"),FACE);
            var sketch = newSketch(context, id + "F74", { "sketchPlane" : qUnion([Q0])});
            skLineSegment(sketch, "E134", {"start": v(0, 0) * mm, "end": v(4500, 0) * mm});
            skLineSegment(sketch, "E135", {"start": v(4500, 0) * mm, "end": v(4500, 1000) * mm});
            skLineSegment(sketch, "E136", {"start": v(4500, 1000) * mm, "end": v(4500, 750) * mm});
            skLineSegment(sketch, "E137", {"start": v(4500, 750) * mm, "end": v(4000, 750) * mm});
            skLineSegment(sketch, "E138", {"start": v(4500, 750) * mm, "end": v(6250, 750) * mm});
            skLineSegment(sketch, "E139", {"start": v(4500, 1000) * mm, "end": v(4000, 1000) * mm});
            skLineSegment(sketch, "E140", {"start": v(4500, 1000) * mm, "end": v(6881.46, 1000) * mm});
            skLineSegment(sketch, "E141", {"start": v(6881.46, 1000) * mm, "end": v(8500, 1000) * mm});
            skLineSegment(sketch, "E142", {"start": v(8500, 1000) * mm, "end": v(8500, 2800) * mm});
            skLineSegment(sketch, "E143", {"start": v(6881.46, 1000) * mm, "end": v(7648.6, 2572.89) * mm});
            skLineSegment(sketch, "E144", {"start": v(7648.6, 2572.89) * mm, "end": v(5943.2, 2572.89) * mm});
            skLineSegment(sketch, "E145", {"start": v(5943.2, 2572.89) * mm, "end": v(4000, 1000) * mm});
            skSolve(sketch);
        }
        {
            var Q0;
            Q0=qCreatedBy(makeId("Top.planeOp"),FACE);
            cPlane(context, id + "F75", {"entities" : qUnion([Q0]), "cplaneType" : CPlaneType.OFFSET, "offset" : 750 * mm, "width" : 150 * mm, "height" : 150 * mm});
        }
        {
            var Q0;
            Q0=qCreatedBy(id+"F75.planeOp",FACE);
            var sketch = newSketch(context, id + "F76", { "sketchPlane" : qUnion([Q0])});
            skFitSpline(sketch, "E146", {"points": [v(0, 4000) * mm, v(-250, 4500) * mm, v(0, 6250) * mm], "startDerivative": vector(-889.86, 1147.1) * mm, "endDerivative": vector(737.87, 3164.53) * mm});
            skFitSpline(sketch, "E147", {"points": [v(0, 4000) * mm, v(250, 4500) * mm, v(0, 6250) * mm], "startDerivative": vector(889.86, 1147.1) * mm, "endDerivative": vector(-737.87, 3164.53) * mm});
            skSolve(sketch);
        }
        {
            var Q0;
            Q0=qCreatedBy(makeId("Top.planeOp"),FACE);
            cPlane(context, id + "F77", {"entities" : qUnion([Q0]), "cplaneType" : CPlaneType.OFFSET, "offset" : 1000 * mm, "width" : 150 * mm, "height" : 150 * mm});
        }
        {
            var Q0;
            Q0=qCreatedBy(id+"F77.planeOp",FACE);
            var sketch = newSketch(context, id + "F78", { "sketchPlane" : qUnion([Q0])});
            skFitSpline(sketch, "E148", {"points": [v(0, 4000) * mm, v(-250, 4500) * mm, v(0, 6881.46) * mm], "startDerivative": vector(0, 2302.24) * mm, "endDerivative": vector(0, 5298.17) * mm});
            skFitSpline(sketch, "E149", {"points": [v(0, 4000) * mm, v(250, 4500) * mm, v(0, 6881.46) * mm], "startDerivative": vector(0, 2302.24) * mm, "endDerivative": vector(0, 5298.17) * mm});
            skSolve(sketch);
        }
        {
            var Q0;
            Q0=sQuery(id+"F74.wireOp",EDGE,"E144");
            cPlane(context, id + "F79", {"entities" : qUnion([Q0]), "cplaneType" : CPlaneType.LINE_ANGLE, "offset" : 25 * mm, "angle" : 180 * degree, "width" : 150 * mm, "height" : 150 * mm});
        }
        {
            var Q0;
            Q0=qCreatedBy(id+"F79.planeOp",FACE);
            var sketch = newSketch(context, id + "F80", { "sketchPlane" : qUnion([Q0])});
            skFitSpline(sketch, "E150", {"points": [v(0, 5943.2) * mm, v(-25, 6795.9) * mm, v(0, 7648.6) * mm], "startDerivative": vector(-75, 1705.4) * mm, "endDerivative": vector(75, 1705.4) * mm});
            skFitSpline(sketch, "E151", {"points": [v(0, 5943.2) * mm, v(25, 6795.9) * mm, v(0, 7648.6) * mm], "startDerivative": vector(75, 1705.4) * mm, "endDerivative": vector(-75, 1705.4) * mm});
            skSolve(sketch);
        }
        {
            var Q0;
            Q0=qCreatedBy(makeId("Front.planeOp"),FACE);
            cPlane(context, id + "F81", {"entities" : qUnion([Q0]), "cplaneType" : CPlaneType.OFFSET, "offset" : 8500 * mm, "oppositeDirection" : true, "width" : 150 * mm, "height" : 150 * mm});
        }
        {
            var Q0;
            Q0=qCreatedBy(id+"F81.planeOp",FACE);
            var sketch = newSketch(context, id + "F82", { "sketchPlane" : qUnion([Q0])});
            skCircle(sketch, "E152", {"center": v(0, 2775) * mm, "radius": 25 * mm});
            skSolve(sketch);
        }
        {
            var Q0;
            Q0=qCreatedBy(makeId("Right.planeOp"),FACE);
            var sketch = newSketch(context, id + "F83", { "sketchPlane" : qUnion([Q0])});
            skLineSegment(sketch, "E153", {"start": v(5943.2, 2572.89) * mm, "end": v(8500, 2800) * mm});
            skSolve(sketch);
        }
        {
            var Q1;
            Q1=qSketchRegion(id+"F76",true);
            var Q2;
            Q2=qSketchRegion(id+"F78",true);
            loft(context, id + "F84", {"sheetProfilesArray" : [{ "sheetProfileEntities" : qUnion([Q1]) }, { "sheetProfileEntities" : qUnion([Q2]) }]});
        }
        {
            var Q1;
            {var subQ0=sQuery(id+"F78.wireOp",EDGE,"E148");Q1=makeQuery(id+"F84.opLoft","CAP_FACE",FACE,{"disambiguationData":[OSD([makeQuery(id+"F78.imprint","IMPRINT",FACE,{"disambiguationData":[TD([[makeQuery(id+"F78.imprint","IMPRINT",EDGE,{"derivedFrom":subQ0}),-1.0]])]})])],"isStart":true});}
            var Q2;
            Q2=makeQuery(id+"F80.imprint","IMPRINT",FACE,{"disambiguationData":[TD([[makeQuery(id+"F80.imprint","IMPRINT",EDGE,{"derivedFrom":sQuery(id+"F80.wireOp",EDGE,"E150")}),-1.0]])]});
            loft(context, id + "F85", {"operationType" : NewBodyOperationType.ADD, "sheetProfilesArray" : [{ "sheetProfileEntities" : qUnion([Q1]) }, { "sheetProfileEntities" : qUnion([Q2]) }]});
        }
        {
            var Q1;
            Q1=makeQuery(id+"F85.opLoft","CAP_FACE",FACE,{"disambiguationData":[OSD([makeQuery(id+"F80.imprint","IMPRINT",FACE,{"disambiguationData":[TD([[makeQuery(id+"F80.imprint","IMPRINT",EDGE,{"derivedFrom":sQuery(id+"F80.wireOp",EDGE,"E150")}),-1.0]])]})])],"isStart":true});
            var Q2;
            Q2=makeQuery(id+"F82.imprint","IMPRINT",FACE,{"disambiguationData":[TD([[makeQuery(id+"F82.imprint","IMPRINT",EDGE,{"derivedFrom":sQuery(id+"F82.wireOp",EDGE,"E152")}),1.0]])]});
            var Q3;
            Q3=sQuery(id+"F83.wireOp",EDGE,"E153");
            loft(context, id + "F86", {"operationType" : NewBodyOperationType.ADD, "addGuides" : true, "sheetProfilesArray" : [{ "sheetProfileEntities" : qUnion([Q1]) }, { "sheetProfileEntities" : qUnion([Q2]) }], "guidesArray" : [{ "guideEntities" : qUnion([Q3]), "guideDerivativeType" : LoftGuideDerivativeType.DEFAULT, "guideDerivativeMagnitude" : 1 }]});
        }
        {
            var Q0;
            Q0=qCreatedBy(makeId("Top.planeOp"),FACE);
            cPlane(context, id + "F87", {"entities" : qUnion([Q0]), "cplaneType" : CPlaneType.OFFSET, "offset" : 2000 * mm, "width" : 150 * mm, "height" : 150 * mm});
        }
        {
            var Q0;
            Q0=qCreatedBy(id+"F87.planeOp",FACE);
            var sketch = newSketch(context, id + "F88", { "sketchPlane" : qUnion([Q0])});
            skLineSegment(sketch, "E154", {"start": v(0, 0) * mm, "end": v(0, 4500) * mm});
            skLineSegment(sketch, "E155", {"start": v(0, 4500) * mm, "end": v(0, 7369.2) * mm});
            skLineSegment(sketch, "E156", {"start": v(0, 7369.2) * mm, "end": v(0, 5235.43) * mm});
            skLineSegment(sketch, "E157", {"start": v(0, 6302.31) * mm, "end": v(0, 5302.31) * mm});
            skLineSegment(sketch, "E158", {"start": v(0, 6302.31) * mm, "end": v(0, 7302.31) * mm});
            skLineSegment(sketch, "E159", {"start": v(0, 6302.31) * mm, "end": v(0, 6552.31) * mm});
            skLineSegment(sketch, "E160", {"start": v(0, 6302.31) * mm, "end": v(-1200, 6302.31) * mm});
            skLineSegment(sketch, "E161", {"start": v(0, 6302.31) * mm, "end": v(1200, 6302.31) * mm});
            skLineSegment(sketch, "E162", {"start": v(0, 6552.31) * mm, "end": v(-1700, 6552.31) * mm});
            skLineSegment(sketch, "E163", {"start": v(0, 6552.31) * mm, "end": v(1700, 6552.31) * mm});
            skLineSegment(sketch, "E164", {"start": v(0, 7302.31) * mm, "end": v(-2000, 7302.31) * mm});
            skLineSegment(sketch, "E165", {"start": v(0, 7302.31) * mm, "end": v(2000, 7302.31) * mm});
            skLineSegment(sketch, "E166", {"start": v(-2000, 7302.31) * mm, "end": v(-2000, 7052.31) * mm});
            skLineSegment(sketch, "E167", {"start": v(2000, 7302.31) * mm, "end": v(2000, 7052.31) * mm});
            skFitSpline(sketch, "E168", {"points": [v(0, 5302.31) * mm, v(-1200, 6302.31) * mm, v(-2000, 7052.31) * mm], "startDerivative": vector(0, 5513.6) * mm, "endDerivative": vector(-1974.16, 3290.27) * mm});
            skFitSpline(sketch, "E169", {"points": [v(0, 5302.31) * mm, v(1200, 6302.31) * mm, v(2000, 7052.31) * mm], "startDerivative": vector(0, 5513.6) * mm, "endDerivative": vector(1974.16, 3290.27) * mm});
            skFitSpline(sketch, "E170", {"points": [v(0, 6552.31) * mm, v(-2000, 7302.31) * mm], "startDerivative": vector(0, 2250) * mm, "endDerivative": vector(-900, 2250) * mm});
            skFitSpline(sketch, "E171", {"points": [v(0, 6552.31) * mm, v(2000, 7302.31) * mm], "startDerivative": vector(0, 2250) * mm, "endDerivative": vector(900, 2250) * mm});
            skSolve(sketch);
        }
        {
            var Q0;
            Q0=qCreatedBy(makeId("Right.planeOp"),FACE);
            var sketch = newSketch(context, id + "F89", { "sketchPlane" : qUnion([Q0])});
            skFitSpline(sketch, "E172", {"points": [v(5302.31, 2000) * mm, v(5927.31, 2050) * mm, v(6552.31, 2000) * mm], "startDerivative": vector(1250, 150) * mm, "endDerivative": vector(1250, -150) * mm});
            skFitSpline(sketch, "E173", {"points": [v(5302.31, 2000) * mm, v(5927.31, 1950) * mm, v(6552.31, 2000) * mm], "startDerivative": vector(1250, -150) * mm, "endDerivative": vector(1250, 150) * mm});
            skSolve(sketch);
        }
        {
            var Q0;
            Q0=qCreatedBy(makeId("Right.planeOp"),FACE);
            cPlane(context, id + "F90", {"entities" : qUnion([Q0]), "cplaneType" : CPlaneType.OFFSET, "offset" : 2000 * mm, "oppositeDirection" : true, "width" : 150 * mm, "height" : 150 * mm});
        }
        {
            var Q0;
            Q0=qCreatedBy(id+"F90.planeOp",FACE);
            var sketch = newSketch(context, id + "F91", { "sketchPlane" : qUnion([Q0])});
            skFitSpline(sketch, "E174", {"points": [v(7052.31, 2000) * mm, v(7177.31, 2010) * mm, v(7302.31, 2000) * mm], "startDerivative": vector(250, 30) * mm, "endDerivative": vector(250, -30) * mm});
            skFitSpline(sketch, "E175", {"points": [v(7052.31, 2000) * mm, v(7177.31, 1990) * mm, v(7302.31, 2000) * mm], "startDerivative": vector(250, -30) * mm, "endDerivative": vector(250, 30) * mm});
            skSolve(sketch);
        }
        {
            var Q0;
            Q0=qCreatedBy(makeId("Right.planeOp"),FACE);
            cPlane(context, id + "F92", {"entities" : qUnion([Q0]), "cplaneType" : CPlaneType.OFFSET, "offset" : 2000 * mm, "width" : 150 * mm, "height" : 150 * mm});
        }
        {
            var Q0;
            Q0=qCreatedBy(id+"F92.planeOp",FACE);
            var sketch = newSketch(context, id + "F93", { "sketchPlane" : qUnion([Q0])});
            skFitSpline(sketch, "E176", {"points": [v(7052.31, 2000) * mm, v(7177.31, 2010) * mm, v(7302.31, 2000) * mm], "startDerivative": vector(250, 30) * mm, "endDerivative": vector(250, -30) * mm});
            skFitSpline(sketch, "E177", {"points": [v(7052.31, 2000) * mm, v(7177.31, 1990) * mm, v(7302.31, 2000) * mm], "startDerivative": vector(250, -30) * mm, "endDerivative": vector(250, 30) * mm});
            skSolve(sketch);
        }
        {
            var Q1;
            Q1=qSketchRegion(id+"F89",true);
            var Q2;
            Q2=makeQuery(id+"F91.imprint","IMPRINT",FACE,{"disambiguationData":[TD([[makeQuery(id+"F91.imprint","IMPRINT",EDGE,{"derivedFrom":sQuery(id+"F91.wireOp",EDGE,"E174")}),-1.0]])]});
            var Q3;
            Q3=sQuery(id+"F88.wireOp",EDGE,"E168");
            var Q4;
            Q4=sQuery(id+"F88.wireOp",EDGE,"E170");
            loft(context, id + "F94", {"addGuides" : true, "sheetProfilesArray" : [{ "sheetProfileEntities" : qUnion([Q1]) }, { "sheetProfileEntities" : qUnion([Q2]) }], "guidesArray" : [{ "guideEntities" : qUnion([Q3]), "guideDerivativeType" : LoftGuideDerivativeType.DEFAULT, "guideDerivativeMagnitude" : 1 }, { "guideEntities" : qUnion([Q4]), "guideDerivativeType" : LoftGuideDerivativeType.DEFAULT, "guideDerivativeMagnitude" : 1 }]});
        }
        {
            var Q1;
            Q1=qSketchRegion(id+"F89",true);
            var Q2;
            Q2=makeQuery(id+"F93.imprint","IMPRINT",FACE,{"disambiguationData":[TD([[makeQuery(id+"F93.imprint","IMPRINT",EDGE,{"derivedFrom":sQuery(id+"F93.wireOp",EDGE,"E176")}),-1.0]])]});
            var Q3;
            Q3=sQuery(id+"F88.wireOp",EDGE,"E169");
            var Q4;
            Q4=sQuery(id+"F88.wireOp",EDGE,"E171");
            loft(context, id + "F95", {"operationType" : NewBodyOperationType.ADD, "addGuides" : true, "sheetProfilesArray" : [{ "sheetProfileEntities" : qUnion([Q1]) }, { "sheetProfileEntities" : qUnion([Q2]) }], "guidesArray" : [{ "guideEntities" : qUnion([Q3]), "guideDerivativeType" : LoftGuideDerivativeType.DEFAULT, "guideDerivativeMagnitude" : 1 }, { "guideEntities" : qUnion([Q4]), "guideDerivativeType" : LoftGuideDerivativeType.DEFAULT, "guideDerivativeMagnitude" : 1 }]});
        }
    });
